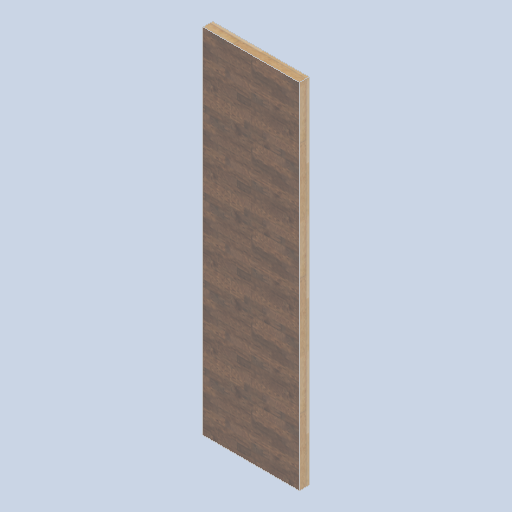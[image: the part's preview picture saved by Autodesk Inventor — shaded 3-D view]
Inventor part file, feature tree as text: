
AUTODESK INVENTOR PART (.ipt)
format: ipt  version: 2024.2 (Build 282272000, 272)  size: 162,816 bytes
history: native  units: in
note: dims shown in document units (in); Inventor stores cm internally (conversion verified against a paired STEP export)
features: other x3, sketch x1
ambient origin geometry x8: Origin, YZ Plane, XZ Plane, XY Plane, X Axis, Y Axis, Z Axis, Center Point
bodies: Solid1 (feature_tree)
feature tree (4):
  other  "front_wall_block04.ipt"
  other  "Solid1::front_wall_block04.ipt"
  other  "TaggingFeature1"
  sketch  "Sketch1"  dims[d0=0.3937in]
